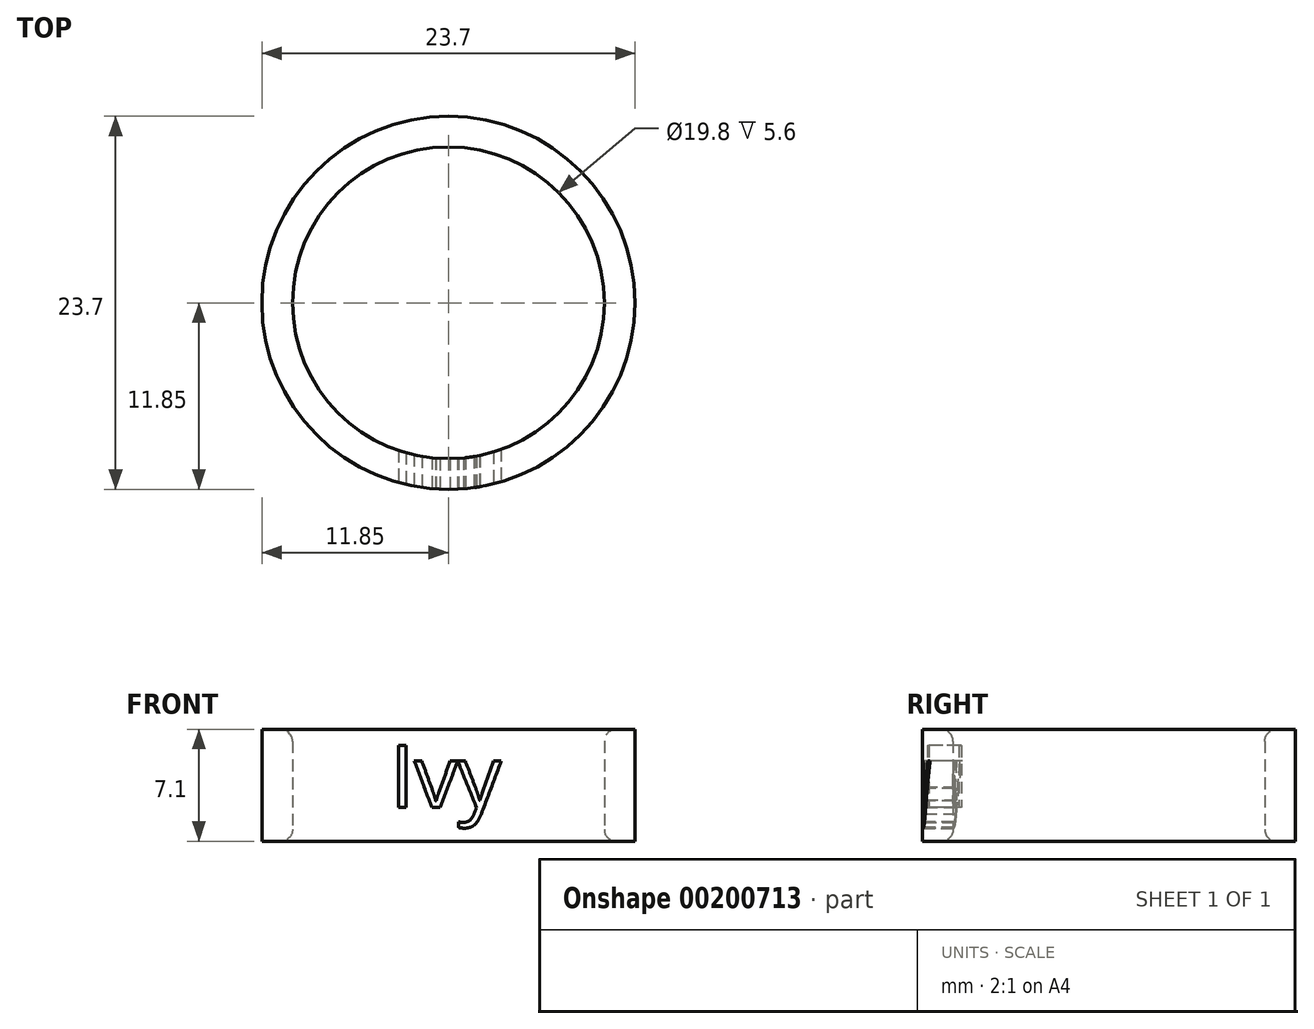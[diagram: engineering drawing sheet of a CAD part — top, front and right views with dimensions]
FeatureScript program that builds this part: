
annotation { "Feature Type Name" : "Feature", "Feature Type Description" : "" }
export const myFeature = defineFeature(function(context is Context, id is Id, definition is map)
    precondition{}
    {
        {
            var Q0;
            Q0=qCreatedBy(makeId("Top.planeOp"),FACE);
            var sketch = newSketch(context, id + "F0", { "sketchPlane" : qUnion([Q0])});
            skCircle(sketch, "E0", {"center": v(0, 0) * mm, "radius": 9.9 * mm});
            skCircle(sketch, "E1.0", {"center": v(0, 0) * mm, "radius": 11.85 * mm});
            skSolve(sketch);
        }
        {
            var Q0;
            Q0=qSketchRegion(id+"F0",true);
            extrude(context, id + "F1", {"entities" : qUnion([Q0]), "depth" : 7.1 * mm});
        }
        {
            var Q0;
            Q0=qCreatedBy(makeId("Front.planeOp"),FACE);
            cPlane(context, id + "F2", {"entities" : qUnion([Q0]), "cplaneType" : CPlaneType.OFFSET, "offset" : 11.85 * mm, "width" : 150 * mm, "height" : 150 * mm});
        }
        {
            var Q0;
            Q0=qCreatedBy(id+"F2.planeOp",FACE);
            var sketch = newSketch(context, id + "F3", { "sketchPlane" : qUnion([Q0])});
            skText(sketch, "E2", { "text": "Ivy", "fontName": "OpenSans-Regular.ttf"});
            skLineSegment(sketch, "E3", {"start": v(-11.85, 0) * mm, "end": v(-11.85, 7.1) * mm});
            skPoint(sketch, "E4.0", {"position": v(0, 0) * mm});
            const initialGuessF3  = {"E2": [-0.0037, 0.00215, 1, 0, 0.00396]};
            skSetInitialGuess(sketch, initialGuessF3);
            skSolve(sketch);
        }
        {
            var Q0;
            Q0 = qSketchRegion(id + "F3", true);
            extrude(context, id + "F4", {"entities" : qUnion([Q0]), "operationType" : NewBodyOperationType.REMOVE, "oppositeDirection" : true, "depth" : 10 * mm});
        }
        {
            var Q0;
            Q0=makeQuery(id+"F1.opExtrude","CAP_EDGE",EDGE,{"disambiguationData":[OSD([sQuery(id+"F0.wireOp",EDGE,"E0")])],"isStart":false});
            var Q1;
            Q1=makeQuery(id+"F1.opExtrude","CAP_EDGE",EDGE,{"disambiguationData":[OSD([sQuery(id+"F0.wireOp",EDGE,"E0")])],"isStart":true});
            fillet(context, id + "F5", {"entities" : qUnion([Q0, Q1]), "radius" : 0.75 * mm, "tangentPropagation" : true, "allowEdgeOverflow" : false});
        }
    });
